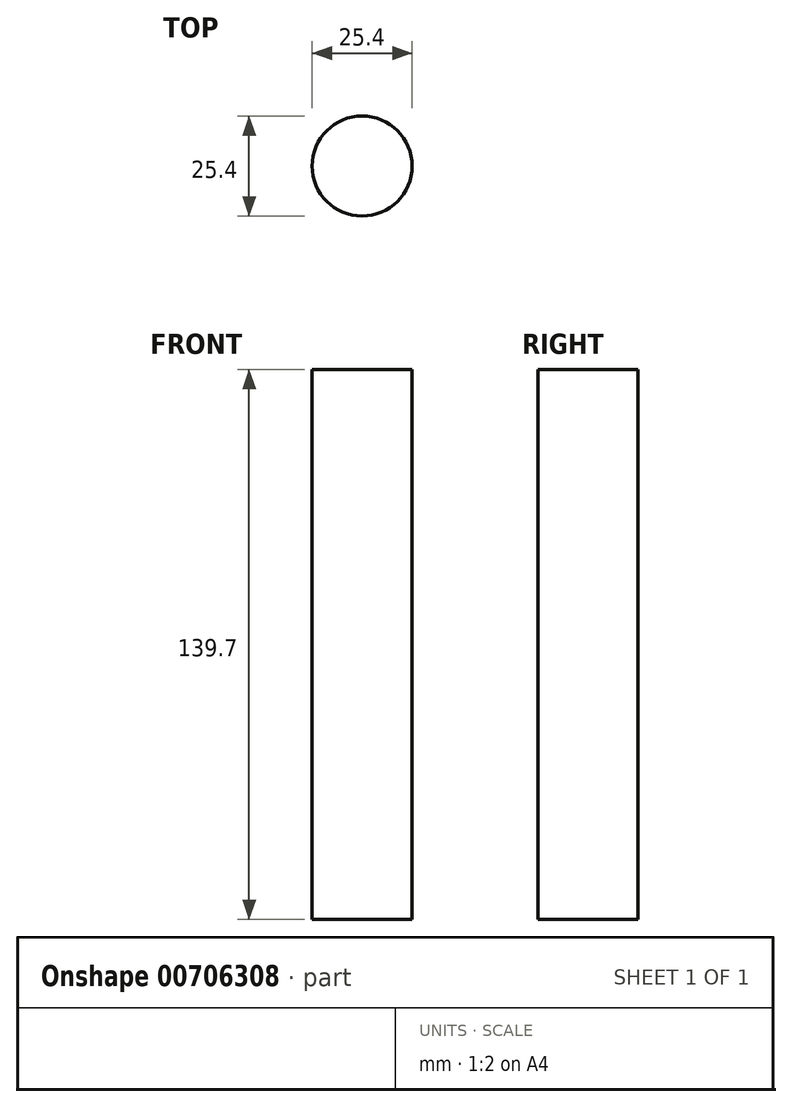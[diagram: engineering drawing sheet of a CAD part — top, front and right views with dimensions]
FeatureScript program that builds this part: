
annotation { "Feature Type Name" : "Feature", "Feature Type Description" : "" }
export const myFeature = defineFeature(function(context is Context, id is Id, definition is map)
    precondition{}
    {
        {
            var Q0;
            Q0=qCreatedBy(makeId("Top.planeOp"),FACE);
            var sketch = newSketch(context, id + "F0", { "sketchPlane" : qUnion([Q0])});
            skCircle(sketch, "E0", {"center": v(0, 0) * mm, "radius": 12.7 * mm});
            skSolve(sketch);
        }
        {
            var Q0;
            Q0 = qSketchRegion(id + "F0", true);
            extrude(context, id + "F1", {"entities" : qUnion([Q0]), "depth" : 139.7 * mm, "offsetDistance" : 25.4 * mm});
        }
    });
